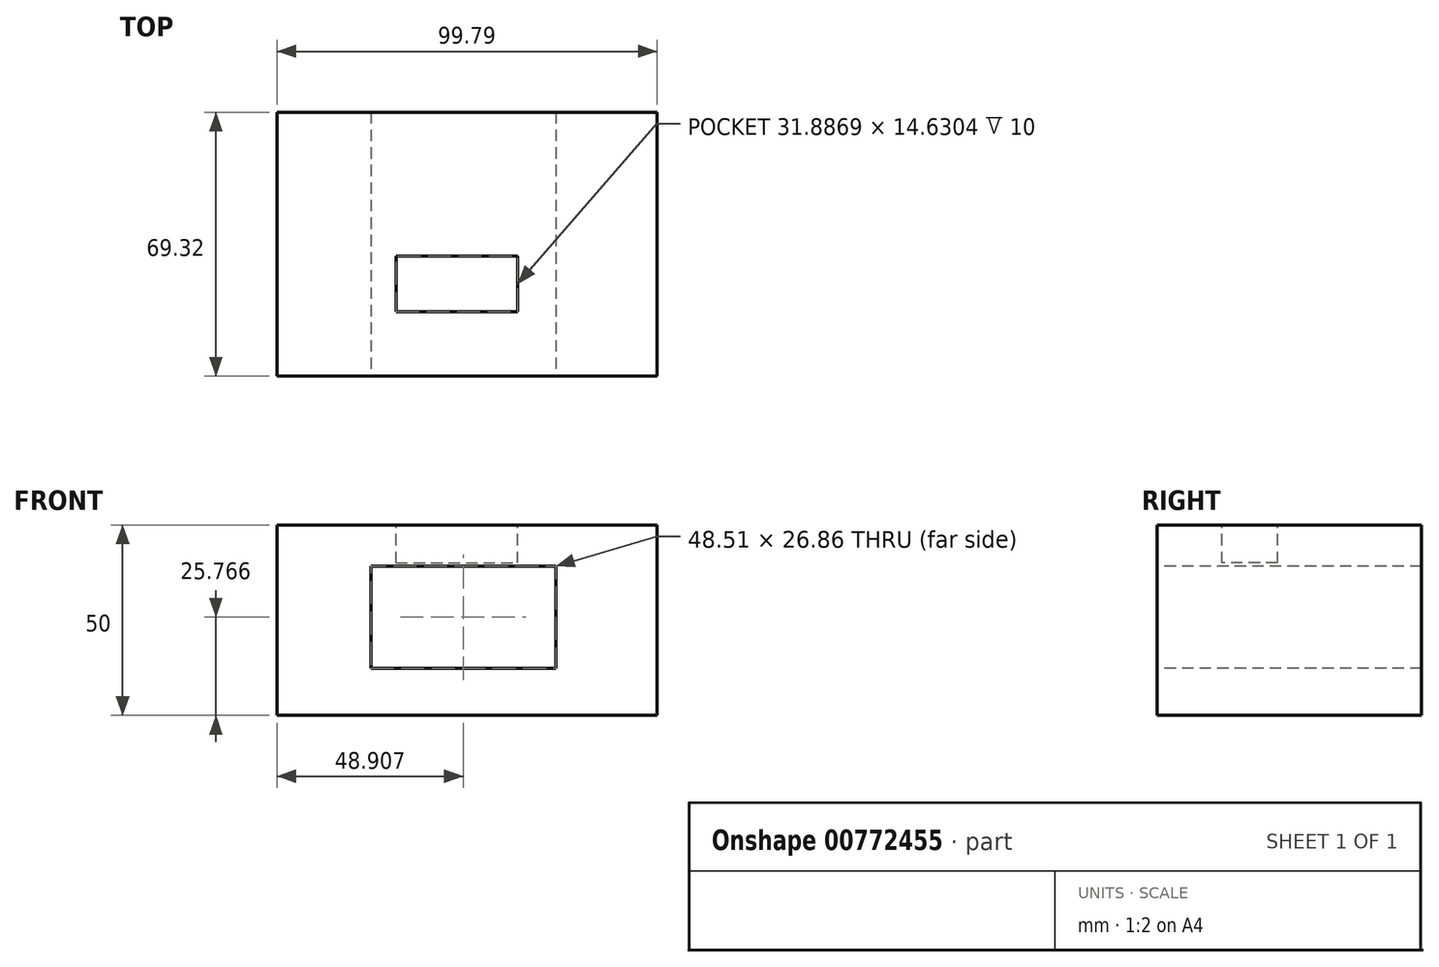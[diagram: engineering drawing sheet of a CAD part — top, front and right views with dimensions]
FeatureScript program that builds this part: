
annotation { "Feature Type Name" : "Feature", "Feature Type Description" : "" }
export const myFeature = defineFeature(function(context is Context, id is Id, definition is map)
    precondition{}
    {
        {
            var Q0;
            Q0=qCreatedBy(makeId("Top.planeOp"),FACE);
            var sketch = newSketch(context, id + "F0", { "sketchPlane" : qUnion([Q0])});
            skLineSegment(sketch, "E0.bottom", {"start": v(-44.18, 33.48) * mm, "end": v(55.61, 33.48) * mm});
            skLineSegment(sketch, "E0.top", {"start": v(-44.18, -35.84) * mm, "end": v(55.61, -35.84) * mm});
            skLineSegment(sketch, "E0.left", {"start": v(-44.18, 33.48) * mm, "end": v(-44.18, -35.84) * mm});
            skLineSegment(sketch, "E0.right", {"start": v(55.61, 33.48) * mm, "end": v(55.61, -35.84) * mm});
            skSolve(sketch);
        }
        {
            var Q0;
            Q0=makeQuery(id+"F0.imprint","IMPRINT",FACE,{"disambiguationData":[TD([[makeQuery(id+"F0.imprint","IMPRINT",EDGE,{"derivedFrom":sQuery(id+"F0.wireOp",EDGE,"E0.bottom")}),-1.0]])]});
            extrude(context, id + "F1", {"entities" : qUnion([Q0]), "depth" : 50 * mm, "offsetDistance" : 25 * mm});
        }
        {
            var Q0;
            Q0=makeQuery(id+"F1.opExtrude","SWEPT_FACE",FACE,{"disambiguationData":[OSD([sQuery(id+"F0.wireOp",EDGE,"E0.top")])]});
            var sketch = newSketch(context, id + "F2", { "sketchPlane" : qUnion([Q0])});
            skLineSegment(sketch, "E1.bottom", {"start": v(-19.53, 39.2) * mm, "end": v(28.98, 39.2) * mm});
            skLineSegment(sketch, "E1.top", {"start": v(-19.53, 12.33) * mm, "end": v(28.98, 12.33) * mm});
            skLineSegment(sketch, "E1.left", {"start": v(-19.53, 39.2) * mm, "end": v(-19.53, 12.33) * mm});
            skLineSegment(sketch, "E1.right", {"start": v(28.98, 39.2) * mm, "end": v(28.98, 12.33) * mm});
            skSolve(sketch);
        }
        {
            var Q0;
            Q0=makeQuery(id+"F2.imprint","IMPRINT",FACE,{"disambiguationData":[TD([[makeQuery(id+"F2.imprint","IMPRINT",EDGE,{"derivedFrom":sQuery(id+"F2.wireOp",EDGE,"E1.bottom")}),-1.0]])]});
            extrude(context, id + "F3", {"entities" : qUnion([Q0]), "operationType" : NewBodyOperationType.REMOVE, "oppositeDirection" : true, "depth" : 100 * mm, "offsetDistance" : 25 * mm});
        }
        {
            var Q0;
            Q0=makeQuery(id+"F3.boolean.opBoolean","COPY",FACE,{"derivedFrom":makeQuery(id+"F3.opExtrude","SWEPT_FACE",FACE,{"disambiguationData":[OSD([sQuery(id+"F2.wireOp",EDGE,"E1.top")])]})});
            var sketch = newSketch(context, id + "F4", { "sketchPlane" : qUnion([Q0])});
            skLineSegment(sketch, "E2.bottom", {"start": v(-10.14, 18.38) * mm, "end": v(-3.04, 18.38) * mm});
            skLineSegment(sketch, "E2.top", {"start": v(-10.14, -23.87) * mm, "end": v(-3.04, -23.87) * mm});
            skLineSegment(sketch, "E2.left", {"start": v(-10.14, 18.38) * mm, "end": v(-10.14, -23.87) * mm});
            skLineSegment(sketch, "E2.right", {"start": v(-3.04, 18.38) * mm, "end": v(-3.04, -23.87) * mm});
            skSolve(sketch);
        }
        {
            var Q0;
            Q0=makeQuery(id+"F3.boolean.opBoolean","COPY",FACE,{"derivedFrom":makeQuery(id+"F3.opExtrude","SWEPT_FACE",FACE,{"disambiguationData":[OSD([sQuery(id+"F2.wireOp",EDGE,"E1.top")])]})});
            var sketch = newSketch(context, id + "F5", { "sketchPlane" : qUnion([Q0])});
            skFitSpline(sketch, "E3", {"points": [v(6.16, 9.8) * mm, v(3.44, -6.04) * mm, v(14.65, -26.72) * mm, v(26.04, 14.02) * mm, v(15.06, 13.8) * mm, v(6.16, 9.8) * mm]});
            skSolve(sketch);
        }
        {
            var Q0;
            Q0=makeQuery(id+"F1.opExtrude","SWEPT_FACE",FACE,{"disambiguationData":[OSD([sQuery(id+"F0.wireOp",EDGE,"E0.right")])]});
            var sketch = newSketch(context, id + "F6", { "sketchPlane" : qUnion([Q0])});
            skLineSegment(sketch, "E4.bottom", {"start": v(-14.18, 34.75) * mm, "end": v(10.53, 34.75) * mm});
            skLineSegment(sketch, "E4.top", {"start": v(-14.18, 15.4) * mm, "end": v(10.53, 15.4) * mm});
            skLineSegment(sketch, "E4.left", {"start": v(-14.18, 34.75) * mm, "end": v(-14.18, 15.4) * mm});
            skLineSegment(sketch, "E4.right", {"start": v(10.53, 34.75) * mm, "end": v(10.53, 15.4) * mm});
            skSolve(sketch);
        }
        {
            var Q0;
            Q0=makeQuery(id+"F1.opExtrude","CAP_FACE",FACE,{"disambiguationData":[OSD([sQuery(id+"F0.wireOp",EDGE,"E0.bottom"),sQuery(id+"F0.wireOp",EDGE,"E0.top"),sQuery(id+"F0.wireOp",EDGE,"E0.left"),sQuery(id+"F0.wireOp",EDGE,"E0.right")])],"isStart":false});
            var sketch = newSketch(context, id + "F7", { "sketchPlane" : qUnion([Q0])});
            skLineSegment(sketch, "E5.bottom", {"start": v(-12.91, -4.3) * mm, "end": v(18.97, -4.3) * mm});
            skLineSegment(sketch, "E5.top", {"start": v(-12.91, -18.93) * mm, "end": v(18.97, -18.93) * mm});
            skLineSegment(sketch, "E5.left", {"start": v(-12.91, -4.3) * mm, "end": v(-12.91, -18.93) * mm});
            skLineSegment(sketch, "E5.right", {"start": v(18.97, -4.3) * mm, "end": v(18.97, -18.93) * mm});
            skSolve(sketch);
        }
        {
            var Q0;
            Q0=makeQuery(id+"F7.imprint","IMPRINT",FACE,{"disambiguationData":[TD([[makeQuery(id+"F7.imprint","IMPRINT",EDGE,{"derivedFrom":sQuery(id+"F7.wireOp",EDGE,"E5.bottom")}),-1.0]])]});
            extrude(context, id + "F8", {"entities" : qUnion([Q0]), "operationType" : NewBodyOperationType.REMOVE, "oppositeDirection" : true, "depth" : 10 * mm, "offsetDistance" : 25 * mm});
        }
    });
